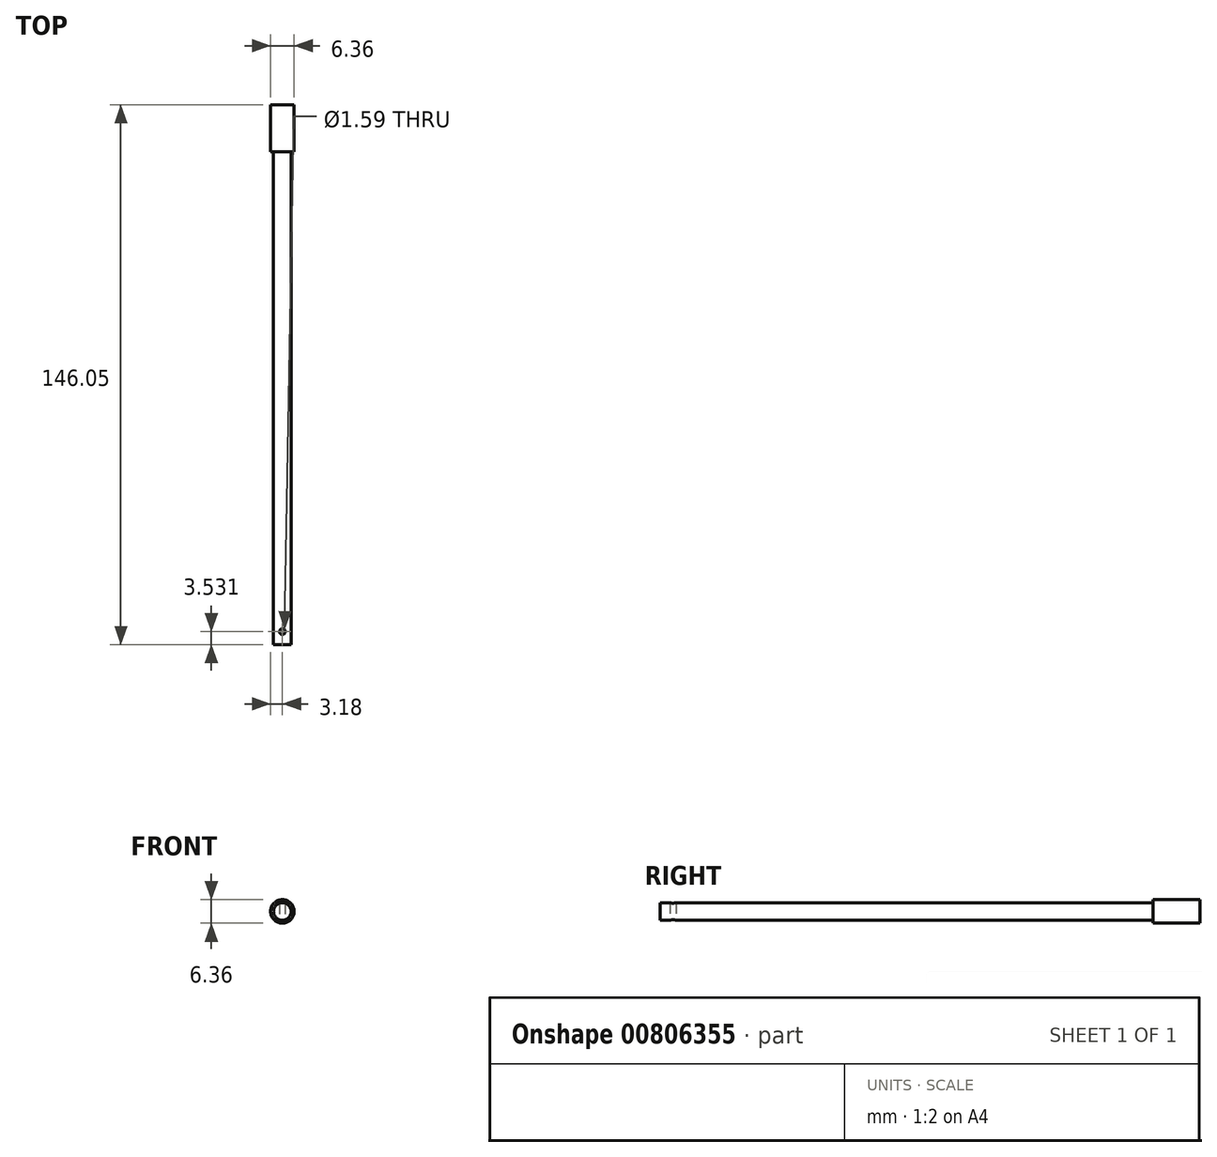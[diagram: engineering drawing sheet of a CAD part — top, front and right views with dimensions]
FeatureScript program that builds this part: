
annotation { "Feature Type Name" : "Feature", "Feature Type Description" : "" }
export const myFeature = defineFeature(function(context is Context, id is Id, definition is map)
    precondition{}
    {
        {
            var Q0;
            Q0=qCreatedBy(makeId("Front.planeOp"),FACE);
            var sketch = newSketch(context, id + "F0", { "sketchPlane" : qUnion([Q0])});
            skCircle(sketch, "E0", {"center": v(0, 0) * mm, "radius": 3.18 * mm});
            skCircle(sketch, "E1", {"center": v(0, 0) * mm, "radius": 2.38 * mm});
            skSolve(sketch);
        }
        {
            var Q0;
            Q0 = qSketchRegion(id + "F0", true);
            extrude(context, id + "F1", {"entities" : qUnion([Q0]), "depth" : 12.7 * mm, "offsetDistance" : 25.4 * mm});
        }
        {
            var Q0;
            Q0=makeQuery(id+"F0.imprint","IMPRINT",FACE,{"disambiguationData":[TD([[makeQuery(id+"F0.imprint","IMPRINT",EDGE,{"derivedFrom":sQuery(id+"F0.wireOp",EDGE,"E1")}),1.0]])]});
            extrude(context, id + "F2", {"entities" : qUnion([Q0]), "operationType" : NewBodyOperationType.ADD, "depth" : 146.05 * mm, "offsetDistance" : 25.4 * mm});
        }
        {
            var Q0;
            Q0=qCreatedBy(makeId("Top.planeOp"),FACE);
            var sketch = newSketch(context, id + "F3", { "sketchPlane" : qUnion([Q0])});
            skLineSegment(sketch, "E2", {"start": v(0, 0) * mm, "end": v(0, -140.61) * mm, "construction": true});
            skCircle(sketch, "E3", {"center": v(0, -142.52) * mm, "radius": 0.8 * mm});
            skSolve(sketch);
        }
        {
            var Q0;
            Q0 = qSketchRegion(id + "F3", true);
            extrude(context, id + "F4", {"entities" : qUnion([Q0]), "operationType" : NewBodyOperationType.REMOVE, "endBound" : BoundingType.SYMMETRIC, "depth" : 6.35 * mm, "offsetDistance" : 25.4 * mm});
        }
    });
